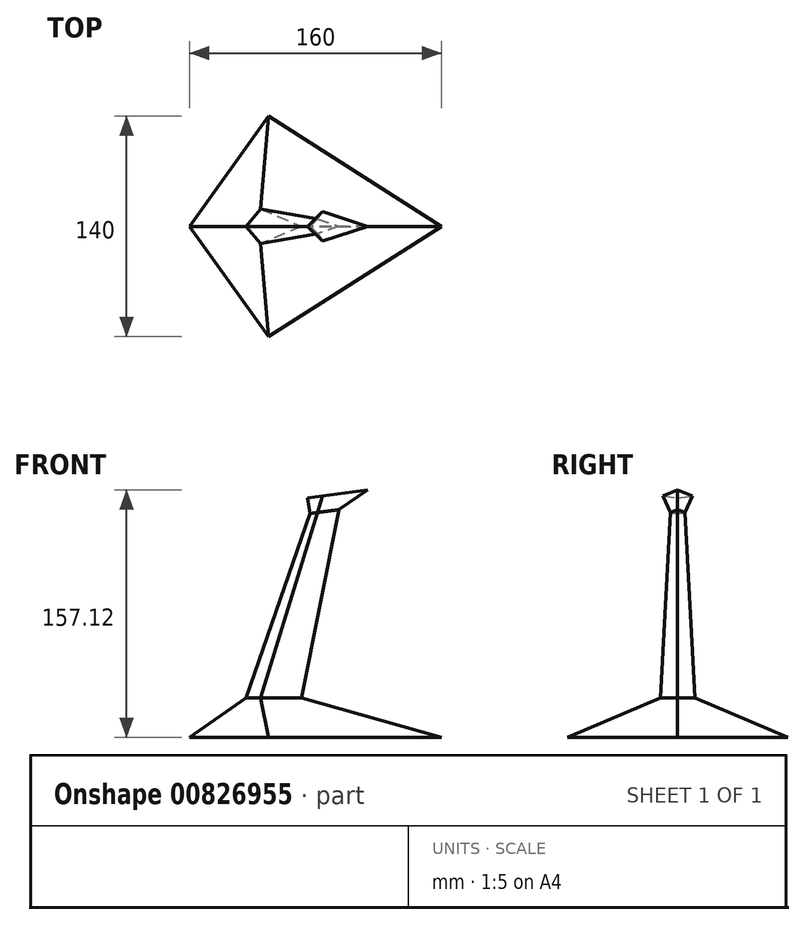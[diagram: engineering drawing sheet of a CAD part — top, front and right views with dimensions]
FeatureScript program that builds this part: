
annotation { "Feature Type Name" : "Feature", "Feature Type Description" : "" }
export const myFeature = defineFeature(function(context is Context, id is Id, definition is map)
    precondition{}
    {
        {
            var Q0;
            Q0=qCreatedBy(makeId("Front.planeOp"),FACE);
            var sketch = newSketch(context, id + "F0", { "sketchPlane" : qUnion([Q0])});
            skLineSegment(sketch, "E0", {"start": v(0, 0) * mm, "end": v(0, 25) * mm});
            skLineSegment(sketch, "E1", {"start": v(0, 25) * mm, "end": v(0, 155) * mm});
            skSolve(sketch);
        }
        {
            var Q0;
            Q0=qCreatedBy(makeId("Top.planeOp"),FACE);
            var sketch = newSketch(context, id + "F1", { "sketchPlane" : qUnion([Q0])});
            skLineSegment(sketch, "E2", {"start": v(-50, 0) * mm, "end": v(0, -70) * mm});
            skLineSegment(sketch, "E3", {"start": v(0, -70) * mm, "end": v(110, 0) * mm});
            skLineSegment(sketch, "E4", {"start": v(110, 0) * mm, "end": v(0, 70) * mm});
            skLineSegment(sketch, "E5", {"start": v(0, 70) * mm, "end": v(-50, 0) * mm});
            skSolve(sketch);
        }
        {
            var Q0;
            Q0=qCreatedBy(makeId("Top.planeOp"),FACE);
            var Q1;
            Q1=sQuery(id+"F0.wireOp",VERTEX,"E0.end");
            cPlane(context, id + "F2", {"entities" : qUnion([Q0, Q1]), "cplaneType" : CPlaneType.PLANE_POINT, "offset" : 0 * mm, "width" : 150 * mm, "height" : 150 * mm});
        }
        {
            var Q0;
            Q0=qCreatedBy(id+"F2.planeOp",FACE);
            var sketch = newSketch(context, id + "F3", { "sketchPlane" : qUnion([Q0])});
            skLineSegment(sketch, "E6", {"start": v(-5, 11) * mm, "end": v(21, 0) * mm});
            skLineSegment(sketch, "E7", {"start": v(21, 0) * mm, "end": v(-5, -11) * mm});
            skLineSegment(sketch, "E8", {"start": v(-5, -11) * mm, "end": v(-14, 0) * mm});
            skLineSegment(sketch, "E9", {"start": v(-14, 0) * mm, "end": v(-5, 11) * mm});
            skSolve(sketch);
        }
        {
            var Q0;
            Q0=makeQuery(id+"F1.imprint","IMPRINT",FACE,{"disambiguationData":[TD([[makeQuery(id+"F1.imprint","IMPRINT",EDGE,{"derivedFrom":sQuery(id+"F1.wireOp",EDGE,"E2")}),1.0]])]});
            var Q1;
            Q1=makeQuery(id+"F3.imprint","IMPRINT",FACE,{"disambiguationData":[TD([[makeQuery(id+"F3.imprint","IMPRINT",EDGE,{"derivedFrom":sQuery(id+"F3.wireOp",EDGE,"E6")}),-1.0]])]});
            loft(context, id + "F4", {"sheetProfilesArray" : [{ "sheetProfileEntities" : qUnion([Q0]) }, { "sheetProfileEntities" : qUnion([Q1]) }]});
        }
        {
            var Q0;
            Q0=qCreatedBy(makeId("Top.planeOp"),FACE);
            var Q1;
            Q1=sQuery(id+"F0.wireOp",VERTEX,"E1.end");
            cPlane(context, id + "F5", {"entities" : qUnion([Q0, Q1]), "cplaneType" : CPlaneType.PLANE_POINT, "offset" : 25 * mm, "width" : 150 * mm, "height" : 150 * mm});
        }
        {
            var Q0;
            Q0=qCreatedBy(id+"F5.planeOp",FACE);
            var sketch = newSketch(context, id + "F6", { "sketchPlane" : qUnion([Q0])});
            skLineSegment(sketch, "E10", {"start": v(31, 0) * mm, "end": v(35, 4) * mm});
            skLineSegment(sketch, "E11", {"start": v(35, 4) * mm, "end": v(47, 0) * mm});
            skLineSegment(sketch, "E12", {"start": v(47, 0) * mm, "end": v(35, -4) * mm});
            skLineSegment(sketch, "E13", {"start": v(35, -4) * mm, "end": v(31, 0) * mm});
            skPoint(sketch, "E14", {"position": v(35, 0) * mm});
            skSolve(sketch);
        }
        {
            var Q1;
            Q1=makeQuery(id+"F4.opLoft","CAP_FACE",FACE,{"disambiguationData":[OSD([makeQuery(id+"F3.imprint","IMPRINT",FACE,{"disambiguationData":[TD([[makeQuery(id+"F3.imprint","IMPRINT",EDGE,{"derivedFrom":sQuery(id+"F3.wireOp",EDGE,"E6")}),-1.0]])]})])],"isStart":true});
            var Q2;
            Q2=makeQuery(id+"F6.imprint","IMPRINT",FACE,{"disambiguationData":[TD([[makeQuery(id+"F6.imprint","IMPRINT",EDGE,{"derivedFrom":sQuery(id+"F6.wireOp",EDGE,"E10")}),-1.0]])]});
            loft(context, id + "F7", {"operationType" : NewBodyOperationType.ADD, "sheetProfilesArray" : [{ "sheetProfileEntities" : qUnion([Q1]) }, { "sheetProfileEntities" : qUnion([Q2]) }]});
        }
        {
            var Q0;
            Q0=qCreatedBy(makeId("Front.planeOp"),FACE);
            var sketch = newSketch(context, id + "F8", { "sketchPlane" : qUnion([Q0])});
            skLineSegment(sketch, "E15", {"start": v(47, 155) * mm, "end": v(30.24, 155) * mm});
            skLineSegment(sketch, "E16", {"start": v(30.24, 155) * mm, "end": v(30.24, 152.8) * mm});
            skLineSegment(sketch, "E17", {"start": v(30.24, 152.8) * mm, "end": v(47, 155) * mm});
            skSolve(sketch);
        }
        {
            var Q0;
            Q0 = qSketchRegion(id + "F8", true);
            extrude(context, id + "F9", {"entities" : qUnion([Q0]), "operationType" : NewBodyOperationType.REMOVE, "endBound" : BoundingType.THROUGH_ALL, "oppositeDirection" : true, "depth" : 25 * mm, "offsetDistance" : 25 * mm, "hasSecondDirection" : true, "secondDirectionBound" : SecondDirectionBoundingType.THROUGH_ALL, "secondDirectionOppositeDirection" : false, "secondDirectionDepth" : 25 * mm});
        }
        {
            var Q0;
            Q0=makeQuery(id+"F9.boolean.opBoolean","COPY",FACE,{"derivedFrom":makeQuery(id+"F9.opExtrude","SWEPT_FACE",FACE,{"disambiguationData":[OSD([sQuery(id+"F8.wireOp",EDGE,"E17")])]})});
            var sketch = newSketch(context, id + "F10", { "sketchPlane" : qUnion([Q0])});
            skLineSegment(sketch, "E18", {"start": v(54.21, 9.34) * mm, "end": v(83.05, 0) * mm});
            skLineSegment(sketch, "E19", {"start": v(83.05, 0) * mm, "end": v(54.21, -9.34) * mm});
            skLineSegment(sketch, "E20", {"start": v(54.21, -9.34) * mm, "end": v(44.4, 0) * mm});
            skLineSegment(sketch, "E21", {"start": v(44.4, 0) * mm, "end": v(54.21, 9.34) * mm});
            skPoint(sketch, "E22", {"position": v(54.21, 0) * mm});
            skLineSegment(sketch, "E23", {"start": v(54.21, 4.09) * mm, "end": v(66.83, 0) * mm, "construction": true});
            skLineSegment(sketch, "E24", {"start": v(66.83, 0) * mm, "end": v(54.21, -4.09) * mm, "construction": true});
            skLineSegment(sketch, "E25", {"start": v(54.21, -4.09) * mm, "end": v(49.92, 0) * mm, "construction": true});
            skLineSegment(sketch, "E26", {"start": v(49.92, 0) * mm, "end": v(54.21, 4.09) * mm, "construction": true});
            skSolve(sketch);
        }
        {
            var Q0;
            Q0=makeQuery(id+"F10.imprint","IMPRINT",FACE,{"disambiguationData":[TD([[makeQuery(id+"F10.imprint","IMPRINT",EDGE,{"derivedFrom":sQuery(id+"F10.wireOp",EDGE,"E18")}),-1.0]])]});
            cPlane(context, id + "F11", {"entities" : qUnion([Q0]), "cplaneType" : CPlaneType.OFFSET, "offset" : 10 * mm, "oppositeDirection" : true, "width" : 150 * mm, "height" : 150 * mm});
        }
        {
            var Q0;
            Q0=qCreatedBy(id+"F11.planeOp",FACE);
            var sketch = newSketch(context, id + "F12", { "sketchPlane" : qUnion([Q0])});
            skLineSegment(sketch, "E27", {"start": v(63.42, 0) * mm, "end": v(49.64, -4.65) * mm});
            skLineSegment(sketch, "E28", {"start": v(49.64, -4.65) * mm, "end": v(44.91, 0) * mm});
            skLineSegment(sketch, "E29", {"start": v(44.91, 0) * mm, "end": v(49.64, 4.65) * mm});
            skLineSegment(sketch, "E30", {"start": v(49.64, 4.65) * mm, "end": v(63.42, 0) * mm});
            skSolve(sketch);
        }
        {
            var Q0;
            Q0=makeQuery(id+"F10.imprint","IMPRINT",FACE,{"disambiguationData":[TD([[makeQuery(id+"F10.imprint","IMPRINT",EDGE,{"derivedFrom":sQuery(id+"F10.wireOp",EDGE,"E18")}),-1.0]])]});
            var sketch = newSketch(context, id + "F13", { "sketchPlane" : qUnion([Q0])});
            skLineSegment(sketch, "E31", {"start": v(54.21, 9.34) * mm, "end": v(44.4, 0) * mm});
            skLineSegment(sketch, "E32", {"start": v(44.4, 0) * mm, "end": v(54.21, -9.34) * mm});
            skLineSegment(sketch, "E33", {"start": v(54.21, -9.34) * mm, "end": v(83.05, 0) * mm});
            skLineSegment(sketch, "E34", {"start": v(83.05, 0) * mm, "end": v(54.21, 9.34) * mm});
            skSolve(sketch);
        }
        {
            var Q0;
            Q0=qCreatedBy(id+"F11.planeOp",FACE);
            var sketch = newSketch(context, id + "F14", { "sketchPlane" : qUnion([Q0])});
            skLineSegment(sketch, "E35.bottom", {"start": v(44.91, 15) * mm, "end": v(84.91, 15) * mm});
            skLineSegment(sketch, "E35.top", {"start": v(44.91, -15) * mm, "end": v(84.91, -15) * mm});
            skLineSegment(sketch, "E35.left", {"start": v(44.91, 15) * mm, "end": v(44.91, -15) * mm});
            skLineSegment(sketch, "E35.right", {"start": v(84.91, 15) * mm, "end": v(84.91, -15) * mm});
            skSolve(sketch);
        }
        {
            var Q0;
            Q0 = qSketchRegion(id + "F14", true);
            extrude(context, id + "F15", {"entities" : qUnion([Q0]), "operationType" : NewBodyOperationType.REMOVE, "depth" : 25 * mm, "offsetDistance" : 25 * mm});
        }
        {
            var Q1;
            Q1=makeQuery(id+"F12.imprint","IMPRINT",FACE,{"disambiguationData":[TD([[makeQuery(id+"F12.imprint","IMPRINT",EDGE,{"derivedFrom":sQuery(id+"F12.wireOp",EDGE,"E27")}),-1.0]])]});
            var Q2;
            Q2 = qSketchRegion(id + "F13", true);
            var Q3;
            Q3=sQuery(id+"F13.wireOp",VERTEX,"E32.end");
            var Q4;
            Q4=sQuery(id+"F12.wireOp",VERTEX,"E27.end");
            loft(context, id + "F16", {"operationType" : NewBodyOperationType.ADD, "sheetProfilesArray" : [{ "sheetProfileEntities" : qUnion([Q1]) }, { "sheetProfileEntities" : qUnion([Q2]) }], "matchConnections" : true, "connections" : [{ "connectionEntities" : qUnion([Q3, Q4]), "connectionEdgeQueries" : qUnion([]), "connectionEdgeParameters" : [] }]});
        }
    });
